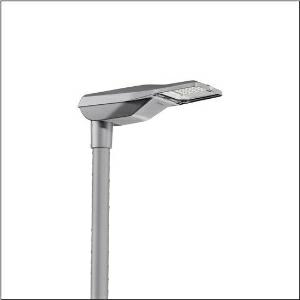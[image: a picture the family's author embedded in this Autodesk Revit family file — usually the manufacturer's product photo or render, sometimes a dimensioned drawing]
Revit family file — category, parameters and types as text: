
# Revit family: streetlight_sl_21_iq_micro___st0_8a_5xe1c61d08cb_7ac8
name_source: partatom
category: Lighting Fixtures
units: mm (PartAtom-declared; Revit-internal decimal feet)

## family parameters
Cut with Voids When Loaded = No
Host = Face
Light Source = No
Part Type = Normal
Room Calculation Point = No
Round Connector Dimension = Use Diameter
Shared = No

## types (1)
- --- (1 x LED, 2570 lm, 19.4 W, 2700K)
    Apparent Load = 19 VA
    CIE Flux Codes = 38 75 97 100 100
    Color Rendering = 70
    Color Temperature = 2700K
    Default Elevation = 1800 mm
    Description = Streetlight SL 21 iQ micro, mast luminaire, primary light control with lens, of PMMA, primary optical cover: cover, of toughened safety glass, transparent, light distribution: ST0.8a, light emission: direct distribution, primary light characteristic: asymmetric, installation type: post-top, side-entry, LED, High Power LED, rated luminous flux: 2.570lm, luminous efficacy: 133lm/W, light colour: 727, colour temperature: 2700K, control gear: iQ-Comfort, control: Auto-Match, Temp-Guard, Lumen-Switch, Night-Set, Smart-Wire, Light-Fading, Desk-Remote (wireless, voltage-free reading and setting of iQ features in the workshop via application-optimized NFC function/RFID function), optimised constant luminous flux control (CLO 2.0), pre-setting: linear dimming characteristic, mains connection: 220..240V, AC, 50/60Hz, start of lifetime: 19W, end of service life: 20W, reduction: 10W, luminaire housing, of diecast aluminium, powder-coated, Siteco® metallic grey (DB 702S), corrosivity category C5 mid according to DIN EN ISO 12944, please order mast flange separately, inclination adjustable: 0°, 5°, 10°, 15°, sealing non-destructively replaceable, multi-level sealing system, length: 528mm, width: 235mm, height: 110mm, mast flange for spigot size: 42mm (side-entry): 5XC10008XM4, 60/48mm (side-entry/post-top): 5XC10108XM2, 76/60mm (side-entry/post-top): 5XC10108XM1, protection rating (complete): IP66, insulation class (complete): insulation class II (safety insulation), certification: CE, ENEC, ENEC+, VDE, impact resistance: IK10, permissible operating ambient temperature for outdoor applications: -40..+50°C, standard-compliant lighting for roads and squares, packaging unit: 1 piece

Light Distribution: ST0.8a
    Height = 110 mm
    Lamp = 1 x LED
    Lamp Light Flux = 2570 lm
    Lamp Power = 19.4 W
    Lamp count = 1
    Length = 528 mm
    Luminous efficacy = 132 lm/W
    Manufacturer = Siteco
    ModVariant = No
    Model = 5XE1C61D08CB
    Number of Poles = 1
    OnlyDefault = Yes
    Power Factor = 1
    Product Name = Streetlight SL 21 iQ micro | ST0.8a
    Product group = mast luminaire | pylon top
    ProductGroupID = 6100
    Protection Class = Protection class II
    Protection Degree = IP 66
    RLX_Detail_Level = 1
    RLX_Emergency_Light_Flux = 0 lm
    RLX_Emergency_Type = 0
    RLX_Emergency_Type_DB = No
    RlxData = <blob elided: 98613 chars, md5=f3a79efe>
    Socket = socket
    Standby Power = 0 W
    System Light Flux = 2570 lm
    System Power = 19 W
    Type Comments = factory setting: luminous flux: 100 % | dim-lin: 254 | 387 mA
    Type Image = l_1006881.jpg
    URL = http://relux.com
    VarID = @adj_159799
    Voltage = 0 V
    Weight = 0.00 kg
    Width = 235 mm

## geometry (parser evidence)
native form markers: Blend x4, Sweep x11
no freeform markers — native parametric forms only
